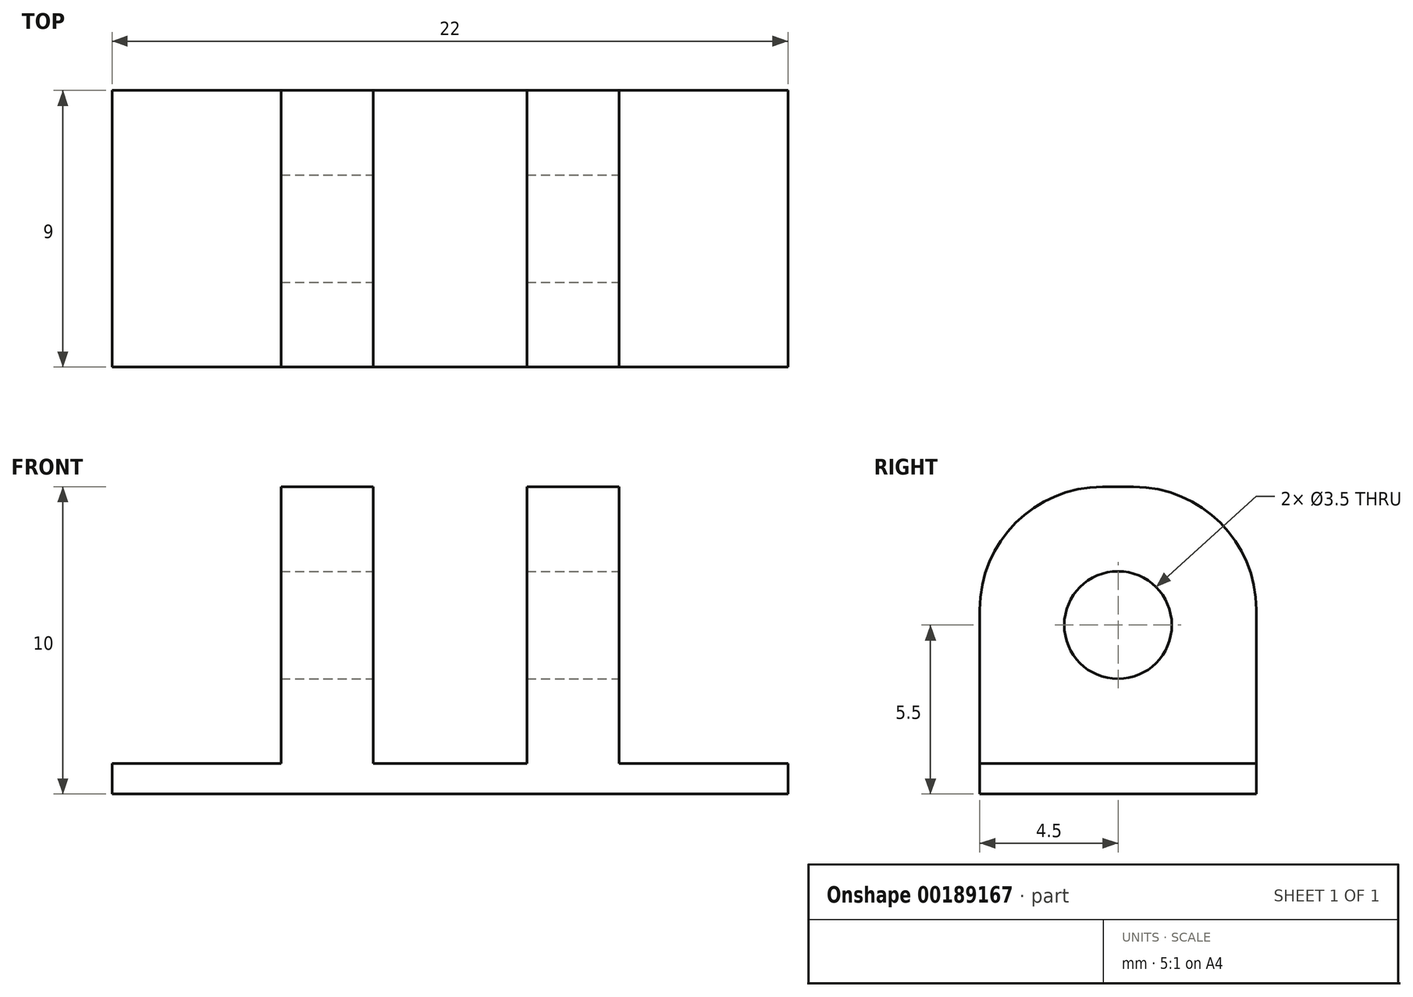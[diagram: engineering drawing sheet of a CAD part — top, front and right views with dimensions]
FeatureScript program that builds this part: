
annotation { "Feature Type Name" : "Feature", "Feature Type Description" : "" }
export const myFeature = defineFeature(function(context is Context, id is Id, definition is map)
    precondition{}
    {
        {
            var Q0;
            Q0=qCreatedBy(makeId("Top.planeOp"),FACE);
            var sketch = newSketch(context, id + "F0", { "sketchPlane" : qUnion([Q0])});
            skLineSegment(sketch, "E0.bottom", {"start": v(-11, 0) * mm, "end": v(11, 0) * mm});
            skLineSegment(sketch, "E0.top", {"start": v(-11, 1) * mm, "end": v(-5.5, 1) * mm});
            skLineSegment(sketch, "E0.left", {"start": v(-11, 0) * mm, "end": v(-11, 1) * mm});
            skLineSegment(sketch, "E0.right", {"start": v(11, 0) * mm, "end": v(11, 1) * mm});
            skLineSegment(sketch, "E1.top", {"start": v(-5.5, 10) * mm, "end": v(-2.5, 10) * mm});
            skLineSegment(sketch, "E1.left", {"start": v(-5.5, 1) * mm, "end": v(-5.5, 10) * mm});
            skLineSegment(sketch, "E1.right", {"start": v(-2.5, 1) * mm, "end": v(-2.5, 10) * mm});
            skLineSegment(sketch, "E2.top", {"start": v(2.5, 10) * mm, "end": v(5.5, 10) * mm});
            skLineSegment(sketch, "E2.left", {"start": v(2.5, 1) * mm, "end": v(2.5, 10) * mm});
            skLineSegment(sketch, "E2.right", {"start": v(5.5, 1) * mm, "end": v(5.5, 10) * mm});
            skLineSegment(sketch, "E3.trimOffspring", {"start": v(5.5, 1) * mm, "end": v(11, 1) * mm});
            skLineSegment(sketch, "E4.trimOffspring", {"start": v(-2.5, 1) * mm, "end": v(2.5, 1) * mm});
            skSolve(sketch);
        }
        {
            var Q0;
            Q0=makeQuery(id+"F0.imprint","IMPRINT",FACE,{"disambiguationData":[TD([[makeQuery(id+"F0.imprint","IMPRINT",EDGE,{"derivedFrom":sQuery(id+"F0.wireOp",EDGE,"E0.bottom")}),1.0]])]});
            extrude(context, id + "F1", {"entities" : qUnion([Q0]), "depth" : 9 * mm});
        }
        {
            var Q0;
            Q0=makeQuery(id+"F1.opExtrude","SWEPT_FACE",FACE,{"disambiguationData":[OSD([sQuery(id+"F0.wireOp",EDGE,"E2.right")])]});
            var sketch = newSketch(context, id + "F2", { "sketchPlane" : qUnion([Q0])});
            skCircle(sketch, "E5", {"center": v(5.5, 4.5) * mm, "radius": 1.75 * mm});
            skPoint(sketch, "E5.centerSnap0", {"position": v(5.5, 9) * mm});
            skPoint(sketch, "E5.centerSnap1", {"position": v(1, 4.5) * mm});
            skSolve(sketch);
        }
        {
            var Q0;
            Q0=makeQuery(id+"F2.imprint","IMPRINT",FACE,{"disambiguationData":[TD([[makeQuery(id+"F2.imprint","IMPRINT",EDGE,{"derivedFrom":sQuery(id+"F2.wireOp",EDGE,"E5")}),1.0]])]});
            extrude(context, id + "F3", {"entities" : qUnion([Q0]), "operationType" : NewBodyOperationType.REMOVE, "oppositeDirection" : true, "depth" : 25 * mm});
        }
        {
            var Q0;
            Q0=makeQuery(id+"F1.opExtrude","CAP_EDGE",EDGE,{"disambiguationData":[OSD([sQuery(id+"F0.wireOp",EDGE,"E1.top")])],"isStart":false});
            var Q1;
            Q1=makeQuery(id+"F1.opExtrude","CAP_EDGE",EDGE,{"disambiguationData":[OSD([sQuery(id+"F0.wireOp",EDGE,"E2.top")])],"isStart":false});
            var Q2;
            Q2=makeQuery(id+"F1.opExtrude","CAP_EDGE",EDGE,{"disambiguationData":[OSD([sQuery(id+"F0.wireOp",EDGE,"E2.top")])],"isStart":true});
            var Q3;
            Q3=makeQuery(id+"F1.opExtrude","CAP_EDGE",EDGE,{"disambiguationData":[OSD([sQuery(id+"F0.wireOp",EDGE,"E1.top")])],"isStart":true});
            fillet(context, id + "F4", {"entities" : qUnion([Q0, Q1, Q2, Q3]), "radius" : 4 * mm, "tangentPropagation" : true, "allowEdgeOverflow" : false});
        }
        {
            var Q0;
            Q0=makeQuery(id+"F1.opExtrude","SWEPT_BODY",BODY,{"disambiguationData":[OSD([sQuery(id+"F0.wireOp",EDGE,"E0.bottom"),sQuery(id+"F0.wireOp",EDGE,"E0.top"),sQuery(id+"F0.wireOp",EDGE,"E0.left"),sQuery(id+"F0.wireOp",EDGE,"E0.right"),sQuery(id+"F0.wireOp",EDGE,"E1.top"),sQuery(id+"F0.wireOp",EDGE,"E1.left"),sQuery(id+"F0.wireOp",EDGE,"E1.right"),sQuery(id+"F0.wireOp",EDGE,"E2.top"),sQuery(id+"F0.wireOp",EDGE,"E2.left"),sQuery(id+"F0.wireOp",EDGE,"E2.right"),sQuery(id+"F0.wireOp",EDGE,"E3.trimOffspring"),sQuery(id+"F0.wireOp",EDGE,"E4.trimOffspring")])]});
            var Q1;
            Q1=makeQuery(id+"F1.opExtrude","CAP_EDGE",EDGE,{"disambiguationData":[OSD([sQuery(id+"F0.wireOp",EDGE,"E0.bottom")])],"isStart":true});
            transform(context, id + "F5", {"entities" : qUnion([Q0]), "transformType" : TransformType.ROTATION, "transformAxis" : qUnion([Q1]), "angle" : 90 * degree, "makeCopy" : false});
        }
    });
